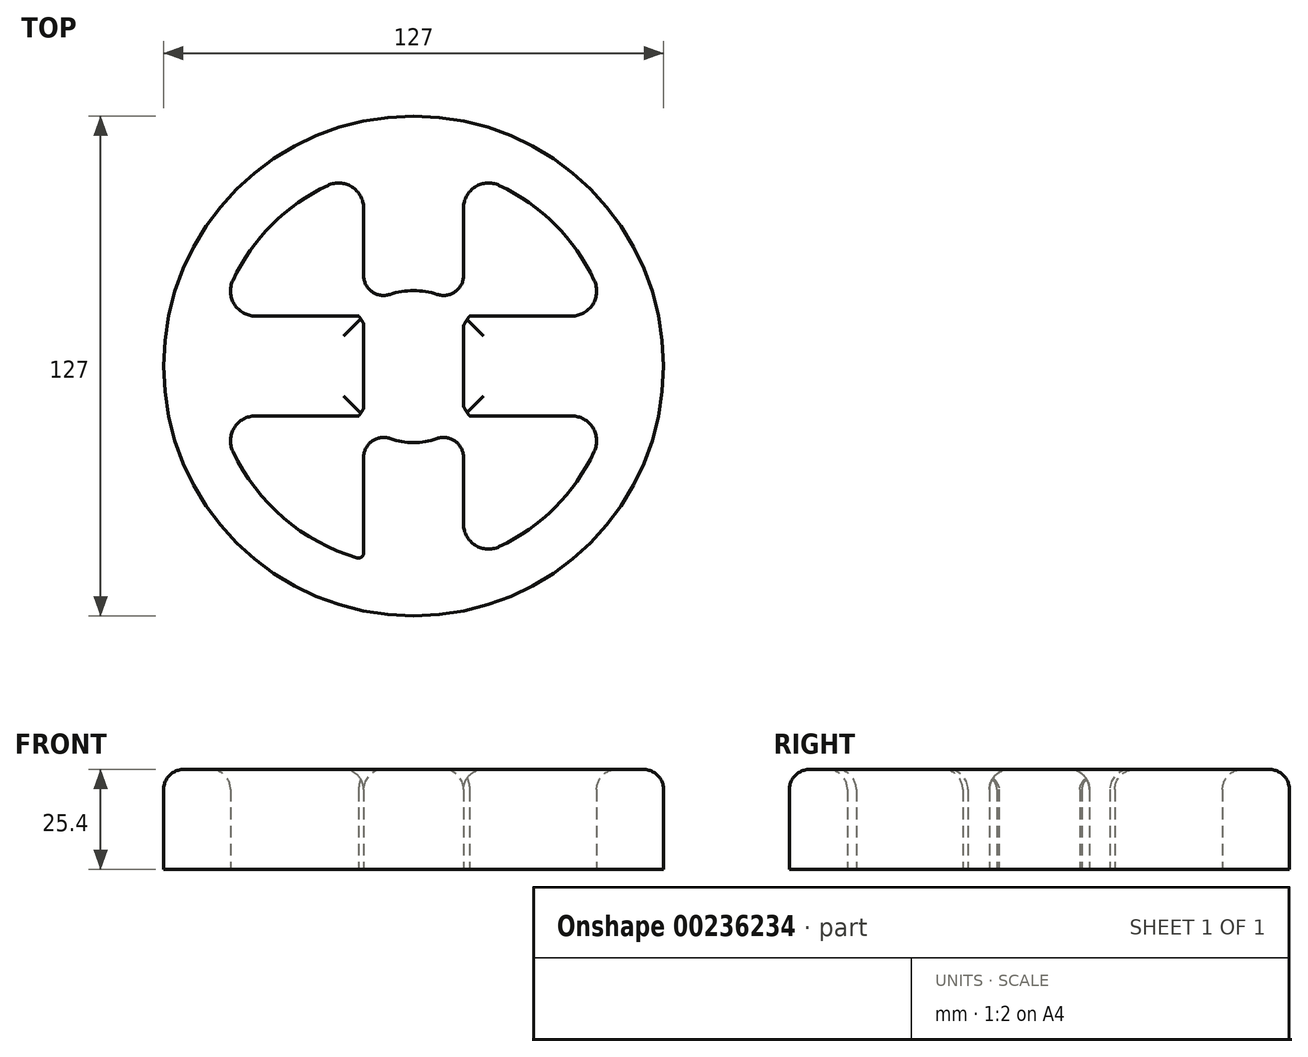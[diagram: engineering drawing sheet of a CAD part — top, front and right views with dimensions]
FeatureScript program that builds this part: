
annotation { "Feature Type Name" : "Feature", "Feature Type Description" : "" }
export const myFeature = defineFeature(function(context is Context, id is Id, definition is map)
    precondition{}
    {
        {
            var Q0;
            Q0=qCreatedBy(makeId("Top.planeOp"),FACE);
            var sketch = newSketch(context, id + "F0", { "sketchPlane" : qUnion([Q0])});
            skCircle(sketch, "E0", {"center": v(0, 0) * mm, "radius": 63.5 * mm});
            skArc(sketch, "E1", {"start": v(21.77, -45.9) * mm, "mid": v(35.92, -35.92) * mm, "end": v(45.9, -21.77) * mm});
            skLineSegment(sketch, "E2", {"start": v(0, 0) * mm, "end": v(0, 50.8) * mm});
            skLineSegment(sketch, "E3.0", {"start": v(12.7, 0) * mm, "end": v(12.7, 40.16) * mm});
            skLineSegment(sketch, "E4.0", {"start": v(-12.7, 0) * mm, "end": v(-12.7, 40.16) * mm});
            skLineSegment(sketch, "E5", {"start": v(0, 0) * mm, "end": v(0, -50.8) * mm});
            skLineSegment(sketch, "E6", {"start": v(0, 0) * mm, "end": v(-50.8, 0) * mm});
            skLineSegment(sketch, "E7", {"start": v(0, 0) * mm, "end": v(50.8, 0) * mm});
            skLineSegment(sketch, "E8.0", {"start": v(0, 12.7) * mm, "end": v(-40.16, 12.7) * mm});
            skLineSegment(sketch, "E9.0", {"start": v(0, -12.7) * mm, "end": v(40.16, -12.7) * mm});
            skLineSegment(sketch, "E10.0", {"start": v(0, 12.7) * mm, "end": v(40.16, 12.7) * mm});
            skLineSegment(sketch, "E11.0", {"start": v(0, -12.7) * mm, "end": v(-40.16, -12.7) * mm});
            skLineSegment(sketch, "E12.trimOffspring", {"start": v(-62.22, 12.7) * mm, "end": v(-63.5, 12.7) * mm});
            skLineSegment(sketch, "E13.trimOffspring", {"start": v(-62.22, -12.7) * mm, "end": v(-63.5, -12.7) * mm});
            skLineSegment(sketch, "E14.trimOffspring", {"start": v(62.22, -12.7) * mm, "end": v(63.5, -12.7) * mm});
            skLineSegment(sketch, "E15.trimOffspring", {"start": v(62.22, 12.7) * mm, "end": v(63.5, 12.7) * mm});
            skLineSegment(sketch, "E16.trimOffspring", {"start": v(12.7, 62.22) * mm, "end": v(12.7, 63.5) * mm});
            skLineSegment(sketch, "E17.trimOffspring", {"start": v(-12.7, 62.22) * mm, "end": v(-12.7, 63.5) * mm});
            skLineSegment(sketch, "E18.0", {"start": v(12.7, 0) * mm, "end": v(12.7, -40.16) * mm});
            skLineSegment(sketch, "E19.0", {"start": v(-12.7, 0) * mm, "end": v(-12.7, -47.52) * mm});
            skArc(sketch, "E20.trimOffspring", {"start": v(-45.9, -21.77) * mm, "mid": v(-33, -38.63) * mm, "end": v(-14.33, -48.74) * mm});
            skArc(sketch, "E21.trimOffspring", {"start": v(-21.77, 45.9) * mm, "mid": v(-35.92, 35.92) * mm, "end": v(-45.9, 21.77) * mm});
            skArc(sketch, "E22.trimOffspring", {"start": v(45.9, 21.77) * mm, "mid": v(35.92, 35.92) * mm, "end": v(21.77, 45.9) * mm});
            skArc(sketch, "E23.trimOffspring", {"start": v(12.7, 14.2) * mm, "mid": v(0, 19.05) * mm, "end": v(-12.7, 14.2) * mm});
            skArc(sketch, "E24.trimOffspring", {"start": v(-12.7, -14.2) * mm, "mid": v(0, -19.05) * mm, "end": v(12.7, -14.2) * mm});
            skPoint(sketch, "E25.visualSharp", {"position": v(-49.19, 12.7) * mm});
            skArc(sketch, "E25.filletArc", {"start": v(-45.9, 21.77) * mm, "mid": v(-45.53, 15.66) * mm, "end": v(-40.16, 12.7) * mm});
            skPoint(sketch, "E26.visualSharp", {"position": v(-49.19, -12.7) * mm});
            skArc(sketch, "E26.filletArc", {"start": v(-40.16, -12.7) * mm, "mid": v(-45.53, -15.66) * mm, "end": v(-45.9, -21.77) * mm});
            skPoint(sketch, "E27.visualSharp", {"position": v(49.19, -12.7) * mm});
            skArc(sketch, "E27.filletArc", {"start": v(45.9, -21.77) * mm, "mid": v(45.53, -15.66) * mm, "end": v(40.16, -12.7) * mm});
            skPoint(sketch, "E28.visualSharp", {"position": v(49.19, 12.7) * mm});
            skArc(sketch, "E28.filletArc", {"start": v(40.16, 12.7) * mm, "mid": v(45.53, 15.66) * mm, "end": v(45.9, 21.77) * mm});
            skPoint(sketch, "E29.visualSharp", {"position": v(12.7, 49.19) * mm});
            skArc(sketch, "E29.filletArc", {"start": v(21.77, 45.9) * mm, "mid": v(15.66, 45.53) * mm, "end": v(12.7, 40.16) * mm});
            skPoint(sketch, "E30.visualSharp", {"position": v(-12.7, 49.19) * mm});
            skArc(sketch, "E30.filletArc", {"start": v(-12.7, 40.16) * mm, "mid": v(-15.66, 45.53) * mm, "end": v(-21.77, 45.9) * mm});
            skArc(sketch, "E31.filletArc", {"start": v(12.7, -40.16) * mm, "mid": v(15.66, -45.53) * mm, "end": v(21.77, -45.9) * mm});
            skArc(sketch, "E32.filletArc", {"start": v(-14.33, -48.74) * mm, "mid": v(-13.2, -48.54) * mm, "end": v(-12.7, -47.52) * mm});
            skLineSegment(sketch, "E33", {"start": v(-14.2, 12.7) * mm, "end": v(-12.7, 14.2) * mm});
            skLineSegment(sketch, "E34", {"start": v(14.2, 12.7) * mm, "end": v(12.7, 14.2) * mm});
            skLineSegment(sketch, "E35", {"start": v(14.2, -12.7) * mm, "end": v(12.7, -14.2) * mm});
            skLineSegment(sketch, "E36", {"start": v(-12.7, -14.2) * mm, "end": v(-14.2, -12.7) * mm});
            skArc(sketch, "E37", {"start": v(-12.7, 49.19) * mm, "mid": v(0, 31.96) * mm, "end": v(12.7, 49.19) * mm});
            skArc(sketch, "E38", {"start": v(49.19, 12.7) * mm, "mid": v(10.1, 0) * mm, "end": v(49.19, -12.7) * mm});
            skArc(sketch, "E39", {"start": v(-49.19, -12.7) * mm, "mid": v(-9.84, 0) * mm, "end": v(-49.19, 12.7) * mm});
            skArc(sketch, "E40", {"start": v(-12.7, 14.2) * mm, "mid": v(-13.4, 13.47) * mm, "end": v(-14.06, 12.7) * mm});
            skArc(sketch, "E41", {"start": v(12.7, -14.2) * mm, "mid": v(13.47, -13.47) * mm, "end": v(14.2, -12.7) * mm});
            skArc(sketch, "E42", {"start": v(14.2, 12.7) * mm, "mid": v(0, 19.05) * mm, "end": v(-14.2, 12.7) * mm});
            skArc(sketch, "E43", {"start": v(-12.7, -14.2) * mm, "mid": v(0, -19.46) * mm, "end": v(12.7, -14.2) * mm});
            skArc(sketch, "E44", {"start": v(-14.21, -12.7) * mm, "mid": v(0, -19.06) * mm, "end": v(14.21, -12.7) * mm});
            skArc(sketch, "E45", {"start": v(14.35, 12.7) * mm, "mid": v(0, 19.17) * mm, "end": v(-14.35, 12.7) * mm});
            skArc(sketch, "E46.trimOffspring", {"start": v(-14.06, -12.7) * mm, "mid": v(-13.4, -13.47) * mm, "end": v(-12.7, -14.2) * mm});
            skArc(sketch, "E47.trimOffspring", {"start": v(-14.35, -12.7) * mm, "mid": v(0, -19.17) * mm, "end": v(14.35, -12.7) * mm});
            skArc(sketch, "E48.trimOffspring", {"start": v(14.21, 12.7) * mm, "mid": v(0, 19.06) * mm, "end": v(-14.21, 12.7) * mm});
            skSolve(sketch);
        }
        {
            var Q0;
            Q0 = qSketchRegion(id + "F0", true);
            extrude(context, id + "F1", {"entities" : qUnion([Q0]), "endBound" : BoundingType.SYMMETRIC, "depth" : 25.4 * mm});
        }
        {
            var Q0;
            Q0=makeQuery(id+"F1.opExtrude","SWEPT_EDGE",EDGE,{"disambiguationData":[OSD([sQuery(id+"F0.wireOp",EDGE,"E3.0"),sQuery(id+"F0.wireOp",EDGE,"E45")])]});
            var Q1;
            Q1=makeQuery(id+"F1.opExtrude","SWEPT_EDGE",EDGE,{"disambiguationData":[OSD([sQuery(id+"F0.wireOp",EDGE,"E4.0"),sQuery(id+"F0.wireOp",EDGE,"E45")])]});
            var Q2;
            Q2=makeQuery(id+"F1.opExtrude","SWEPT_EDGE",EDGE,{"disambiguationData":[OSD([sQuery(id+"F0.wireOp",EDGE,"E18.0"),sQuery(id+"F0.wireOp",EDGE,"E47.trimOffspring")])]});
            var Q3;
            Q3=makeQuery(id+"F1.opExtrude","SWEPT_EDGE",EDGE,{"disambiguationData":[OSD([sQuery(id+"F0.wireOp",EDGE,"E19.0"),sQuery(id+"F0.wireOp",EDGE,"E47.trimOffspring")])]});
            fillet(context, id + "F2", {"entities" : qUnion([Q0, Q1, Q2, Q3]), "radius" : 5.08 * mm, "tangentPropagation" : true, "allowEdgeOverflow" : false});
        }
        {
            var Q0;
            Q0=makeQuery(id+"F1.opExtrude","CAP_FACE",FACE,{"disambiguationData":[OSD([sQuery(id+"F0.wireOp",EDGE,"E0"),sQuery(id+"F0.wireOp",EDGE,"E1"),sQuery(id+"F0.wireOp",EDGE,"E3.0"),sQuery(id+"F0.wireOp",EDGE,"E4.0"),sQuery(id+"F0.wireOp",EDGE,"E8.0"),sQuery(id+"F0.wireOp",EDGE,"E9.0"),sQuery(id+"F0.wireOp",EDGE,"E10.0"),sQuery(id+"F0.wireOp",EDGE,"E11.0"),sQuery(id+"F0.wireOp",EDGE,"E18.0"),sQuery(id+"F0.wireOp",EDGE,"E19.0"),sQuery(id+"F0.wireOp",EDGE,"E20.trimOffspring"),sQuery(id+"F0.wireOp",EDGE,"E21.trimOffspring"),sQuery(id+"F0.wireOp",EDGE,"E22.trimOffspring"),sQuery(id+"F0.wireOp",EDGE,"E25.filletArc"),sQuery(id+"F0.wireOp",EDGE,"E26.filletArc"),sQuery(id+"F0.wireOp",EDGE,"E27.filletArc"),sQuery(id+"F0.wireOp",EDGE,"E28.filletArc"),sQuery(id+"F0.wireOp",EDGE,"E29.filletArc"),sQuery(id+"F0.wireOp",EDGE,"E30.filletArc"),sQuery(id+"F0.wireOp",EDGE,"E31.filletArc"),sQuery(id+"F0.wireOp",EDGE,"E32.filletArc"),sQuery(id+"F0.wireOp",EDGE,"E38"),sQuery(id+"F0.wireOp",EDGE,"E39"),sQuery(id+"F0.wireOp",EDGE,"E43"),sQuery(id+"F0.wireOp",EDGE,"E45"),sQuery(id+"F0.wireOp",EDGE,"E47.trimOffspring")])],"isStart":false});
            fillet(context, id + "F3", {"entities" : qUnion([Q0]), "radius" : 5.08 * mm, "tangentPropagation" : true, "allowEdgeOverflow" : false});
        }
    });
